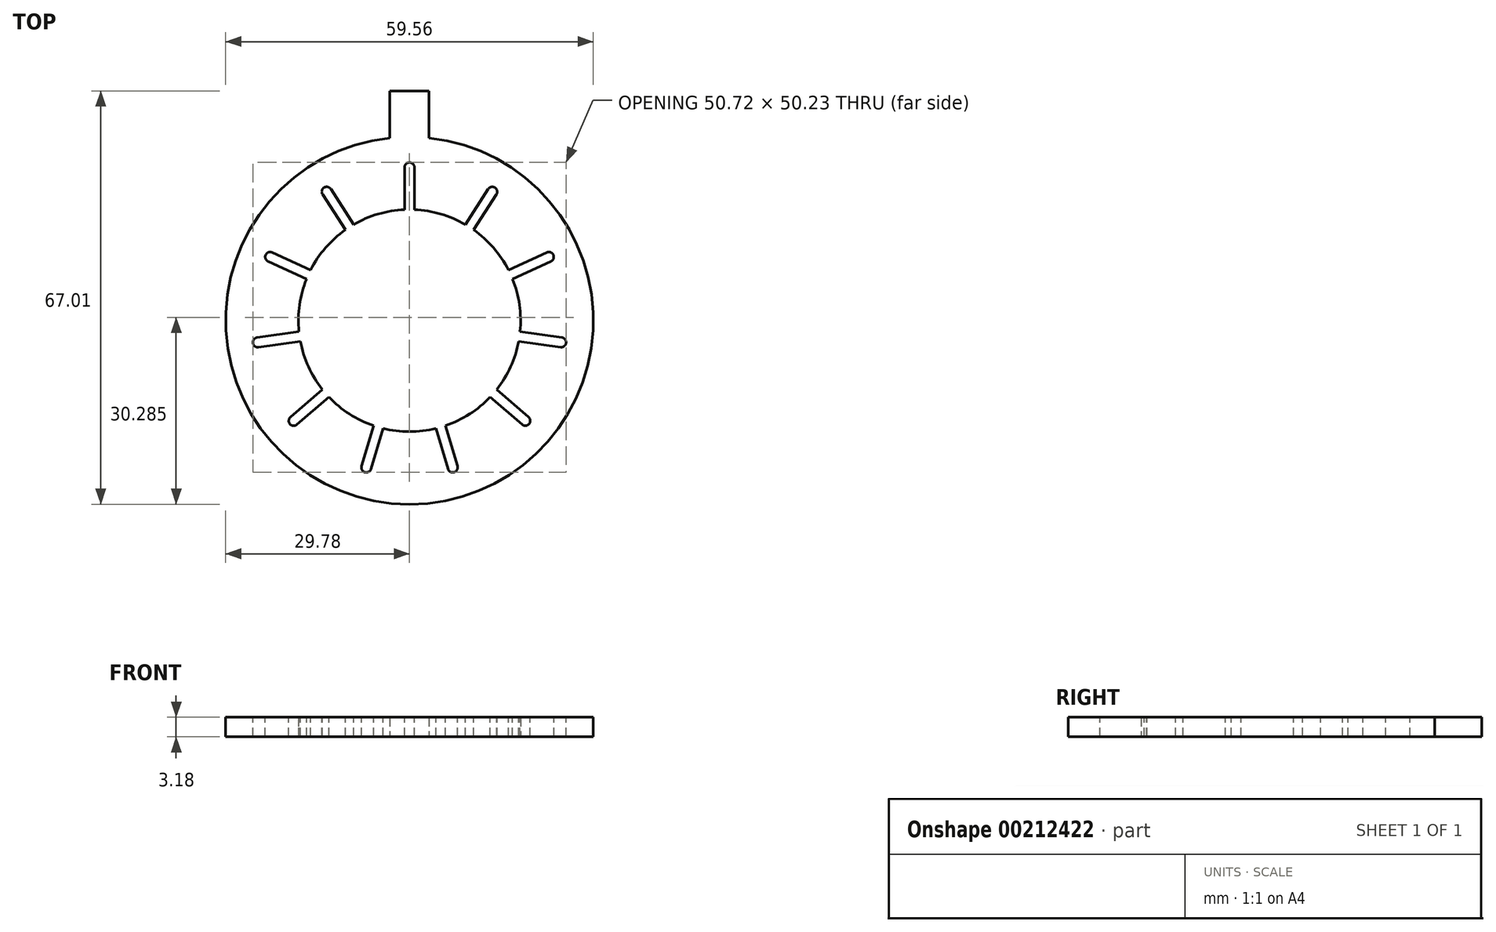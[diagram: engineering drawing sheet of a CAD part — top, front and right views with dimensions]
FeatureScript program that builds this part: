
annotation { "Feature Type Name" : "Feature", "Feature Type Description" : "" }
export const myFeature = defineFeature(function(context is Context, id is Id, definition is map)
    precondition{}
    {
        {
            var Q0;
            Q0=qCreatedBy(makeId("Top.planeOp"),FACE);
            var sketch = newSketch(context, id + "F0", { "sketchPlane" : qUnion([Q0])});
            skCircle(sketch, "E0", {"center": v(0, 0) * mm, "radius": 18 * mm});
            skCircle(sketch, "E1", {"center": v(0, 0) * mm, "radius": 29.78 * mm});
            skSolve(sketch);
        }
        {
            var Q0;
            Q0=qCreatedBy(makeId("Top.planeOp"),FACE);
            var sketch = newSketch(context, id + "F1", { "sketchPlane" : qUnion([Q0])});
            skLineSegment(sketch, "E2.bottom", {"start": v(-3.18, 37.23) * mm, "end": v(3.17, 37.23) * mm});
            skLineSegment(sketch, "E2.top", {"start": v(-3.18, 29.61) * mm, "end": v(3.17, 29.61) * mm});
            skLineSegment(sketch, "E2.left", {"start": v(-3.18, 37.23) * mm, "end": v(-3.18, 29.61) * mm});
            skLineSegment(sketch, "E2.right", {"start": v(3.17, 37.23) * mm, "end": v(3.17, 29.61) * mm});
            skLineSegment(sketch, "E3", {"start": v(0, 0) * mm, "end": v(0, 29.78) * mm, "construction": true});
            skSolve(sketch);
        }
        {
            var Q0;
            Q0=makeQuery(id+"F0.imprint","IMPRINT",FACE,{"disambiguationData":[TD([[makeQuery(id+"F0.imprint","IMPRINT",EDGE,{"derivedFrom":sQuery(id+"F0.wireOp",EDGE,"E0")}),-1.0]])]});
            extrude(context, id + "F2", {"entities" : qUnion([Q0]), "depth" : 3.17 * mm});
        }
        {
            var Q0;
            Q0 = qSketchRegion(id + "F1", true);
            extrude(context, id + "F3", {"entities" : qUnion([Q0]), "operationType" : NewBodyOperationType.ADD, "depth" : 3.17 * mm});
        }
        {
            var Q0;
            Q0=makeQuery(id+"F2.opExtrude","CAP_FACE",FACE,{"disambiguationData":[OSD([sQuery(id+"F0.wireOp",EDGE,"E0"),sQuery(id+"F0.wireOp",EDGE,"E1")])],"isStart":false});
            var sketch = newSketch(context, id + "F4", { "sketchPlane" : qUnion([Q0])});
            skLineSegment(sketch, "E4", {"start": v(0, 25.62) * mm, "end": v(0, 18) * mm, "construction": true});
            skArc(sketch, "E5", {"start": v(0.8, 24.83) * mm, "mid": v(0, 25.62) * mm, "end": v(-0.8, 24.83) * mm});
            skLineSegment(sketch, "E6.top", {"start": v(-0.8, 0) * mm, "end": v(0.8, 0) * mm});
            skLineSegment(sketch, "E6.left", {"start": v(-0.8, 24.83) * mm, "end": v(-0.8, 0) * mm});
            skLineSegment(sketch, "E6.right", {"start": v(0.8, 24.83) * mm, "end": v(0.8, 0) * mm});
            skSolve(sketch);
        }
        {
            var Q0;
            {var subQ0=sQuery(id+"F4.wireOp",EDGE,"E5");Q0=makeQuery(id+"F4.imprint","IMPRINT",FACE,{"disambiguationData":[TD([[makeQuery(id+"F4.imprint","IMPRINT",EDGE,{"derivedFrom":subQ0}),1.0]])]});}
            extrude(context, id + "F5", {"entities" : qUnion([Q0]), "oppositeDirection" : true, "depth" : 25.4 * mm});
        }
        {
            var Q0;
            Q0=makeQuery(id+"F5.opExtrude","SWEPT_BODY",BODY,{"disambiguationData":[OSD([sQuery(id+"F0.wireOp",EDGE,"E0"),sQuery(id+"F4.wireOp",EDGE,"E5"),sQuery(id+"F4.wireOp",EDGE,"E6.left"),sQuery(id+"F4.wireOp",EDGE,"E6.right")])]});
            var Q1;
            Q1=makeQuery(id+"F2.opExtrude","SWEPT_FACE",FACE,{"disambiguationData":[OSD([sQuery(id+"F0.wireOp",EDGE,"E0")])]});
            circularPattern(context, id + "F6", {"operationType" : NewBodyOperationType.REMOVE, "entities" : qUnion([Q0]), "axis" : qUnion([Q1]), "angle" : 360 * degree, "instanceCount" : 11, "equalSpace" : true});
        }
    });
